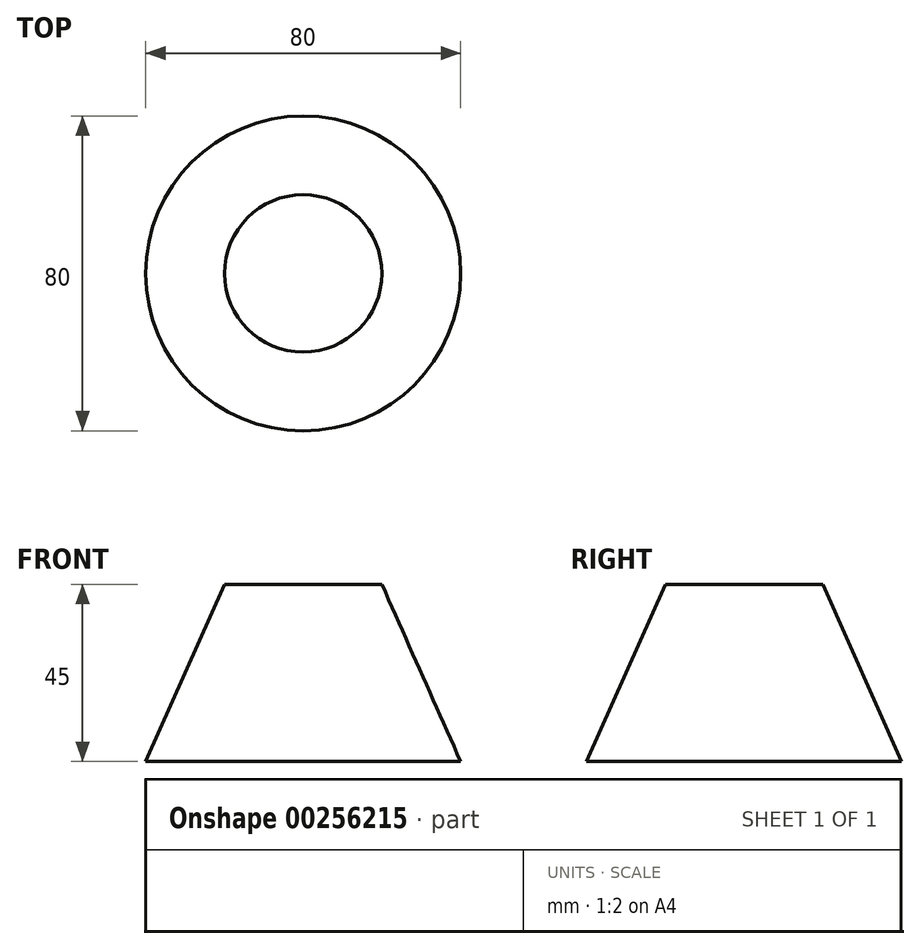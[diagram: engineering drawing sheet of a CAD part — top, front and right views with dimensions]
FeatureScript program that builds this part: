
annotation { "Feature Type Name" : "Feature", "Feature Type Description" : "" }
export const myFeature = defineFeature(function(context is Context, id is Id, definition is map)
    precondition{}
    {
        {
            var Q0;
            Q0=qCreatedBy(makeId("Right.planeOp"),FACE);
            var sketch = newSketch(context, id + "F0", { "sketchPlane" : qUnion([Q0])});
            skLineSegment(sketch, "E0", {"start": v(0, 0) * mm, "end": v(0, 45) * mm});
            skLineSegment(sketch, "E1", {"start": v(20, 45) * mm, "end": v(40, 0) * mm});
            skLineSegment(sketch, "E2", {"start": v(40, 0) * mm, "end": v(0, 0) * mm});
            skLineSegment(sketch, "E3", {"start": v(0, 45) * mm, "end": v(20, 45) * mm});
            skLineSegment(sketch, "E4", {"start": v(0, 66.99) * mm, "end": v(0, -57.8) * mm});
            skLineSegment(sketch, "E5", {"start": v(0, -57.8) * mm, "end": v(0, 66.99) * mm, "construction": true});
            skSolve(sketch);
        }
        {
            var Q0;
            Q0 = qSketchRegion(id + "F0", true);
            var Q1;
            Q1=sQuery(id+"F0.wireOp",EDGE,"E4");
            revolve(context, id + "F1", {"entities" : qUnion([Q0]), "axis" : qUnion([Q1]), "revolveType" : RevolveType.FULL});
        }
    });
